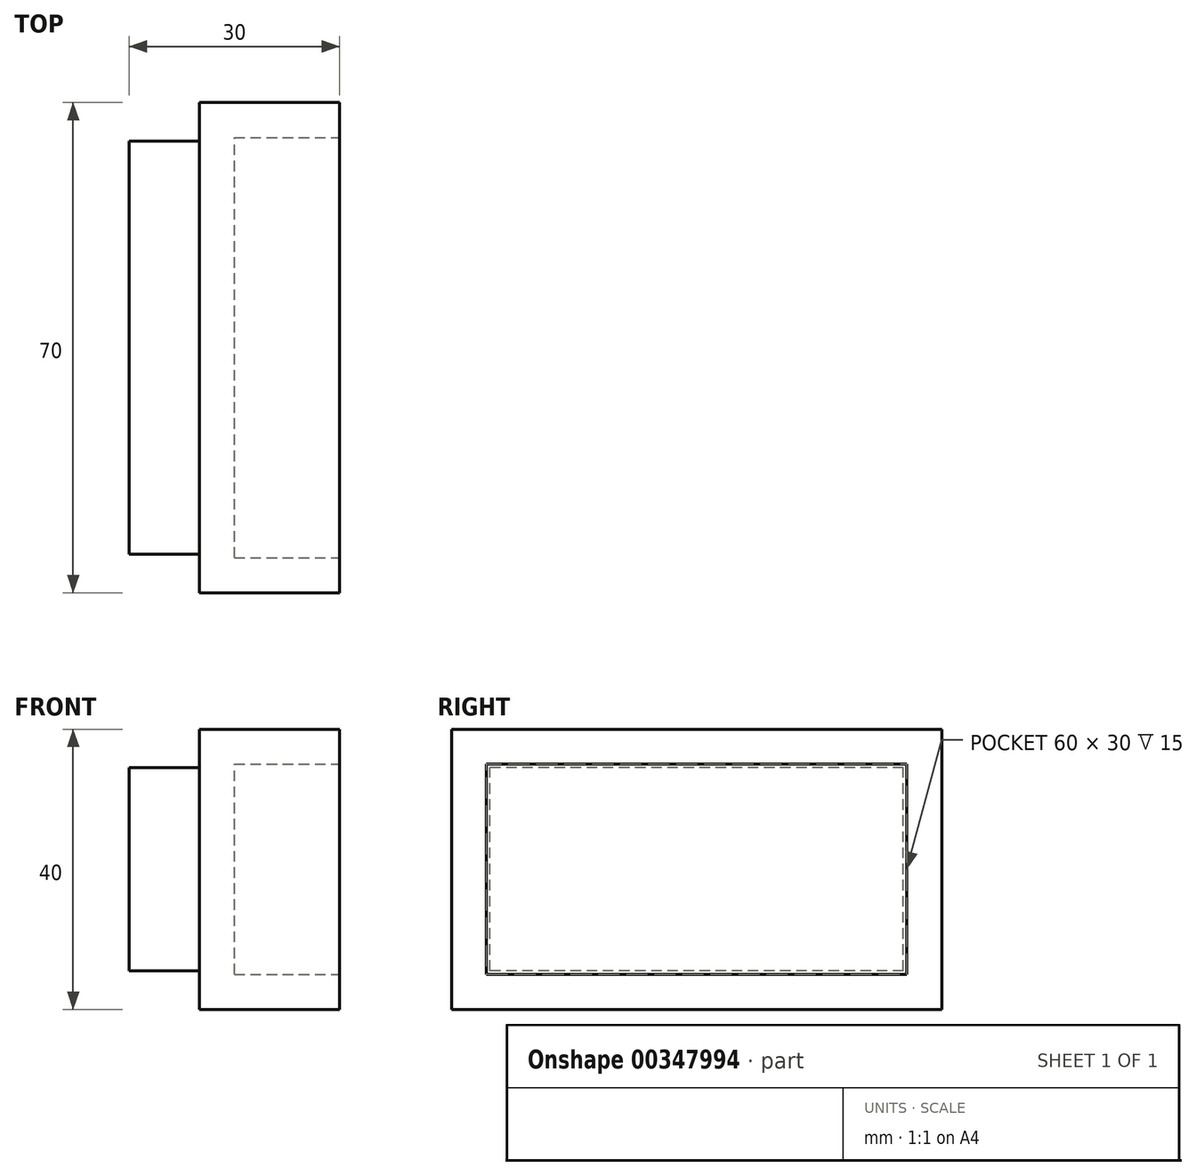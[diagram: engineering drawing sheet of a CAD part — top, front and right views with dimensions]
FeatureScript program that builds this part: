
annotation { "Feature Type Name" : "Feature", "Feature Type Description" : "" }
export const myFeature = defineFeature(function(context is Context, id is Id, definition is map)
    precondition{}
    {
        {
            var Q0;
            Q0=qCreatedBy(makeId("Right.planeOp"),FACE);
            var sketch = newSketch(context, id + "F0", { "sketchPlane" : qUnion([Q0])});
            skLineSegment(sketch, "E0.bottom", {"start": v(0, 0) * mm, "end": v(70, 0) * mm});
            skLineSegment(sketch, "E0.top", {"start": v(0, 40) * mm, "end": v(70, 40) * mm});
            skLineSegment(sketch, "E0.left", {"start": v(0, 0) * mm, "end": v(0, 40) * mm});
            skLineSegment(sketch, "E0.right", {"start": v(70, 0) * mm, "end": v(70, 40) * mm});
            skSolve(sketch);
        }
        {
            var Q0;
            Q0 = qSketchRegion(id + "F0", true);
            extrude(context, id + "F1", {"entities" : qUnion([Q0]), "depth" : 20 * mm});
        }
        {
            var Q0;
            Q0=makeQuery(id+"F1.opExtrude","CAP_FACE",FACE,{"disambiguationData":[OSD([sQuery(id+"F0.wireOp",EDGE,"E0.bottom"),sQuery(id+"F0.wireOp",EDGE,"E0.top"),sQuery(id+"F0.wireOp",EDGE,"E0.left"),sQuery(id+"F0.wireOp",EDGE,"E0.right")])],"isStart":false});
            var sketch = newSketch(context, id + "F2", { "sketchPlane" : qUnion([Q0])});
            skLineSegment(sketch, "E1.bottom", {"start": v(5, 5) * mm, "end": v(65, 5) * mm});
            skLineSegment(sketch, "E1.top", {"start": v(5, 35) * mm, "end": v(65, 35) * mm});
            skLineSegment(sketch, "E1.left", {"start": v(5, 5) * mm, "end": v(5, 35) * mm});
            skLineSegment(sketch, "E1.right", {"start": v(65, 5) * mm, "end": v(65, 35) * mm});
            skSolve(sketch);
        }
        {
            var Q0;
            Q0 = qSketchRegion(id + "F2", true);
            extrude(context, id + "F3", {"entities" : qUnion([Q0]), "operationType" : NewBodyOperationType.REMOVE, "oppositeDirection" : true, "depth" : 15 * mm});
        }
        {
            var Q0;
            Q0=makeQuery(id+"F1.opExtrude","CAP_FACE",FACE,{"disambiguationData":[OSD([sQuery(id+"F0.wireOp",EDGE,"E0.bottom"),sQuery(id+"F0.wireOp",EDGE,"E0.top"),sQuery(id+"F0.wireOp",EDGE,"E0.left"),sQuery(id+"F0.wireOp",EDGE,"E0.right")])],"isStart":true});
            var sketch = newSketch(context, id + "F4", { "sketchPlane" : qUnion([Q0])});
            skLineSegment(sketch, "E2.bottom", {"start": v(-64.5, 5.5) * mm, "end": v(-5.5, 5.5) * mm});
            skLineSegment(sketch, "E2.top", {"start": v(-64.5, 34.5) * mm, "end": v(-5.5, 34.5) * mm});
            skLineSegment(sketch, "E2.left", {"start": v(-64.5, 5.5) * mm, "end": v(-64.5, 34.5) * mm});
            skLineSegment(sketch, "E2.right", {"start": v(-5.5, 5.5) * mm, "end": v(-5.5, 34.5) * mm});
            skSolve(sketch);
        }
        {
            var Q0;
            Q0 = qSketchRegion(id + "F4", true);
            extrude(context, id + "F5", {"entities" : qUnion([Q0]), "operationType" : NewBodyOperationType.ADD, "depth" : 10 * mm});
        }
    });
